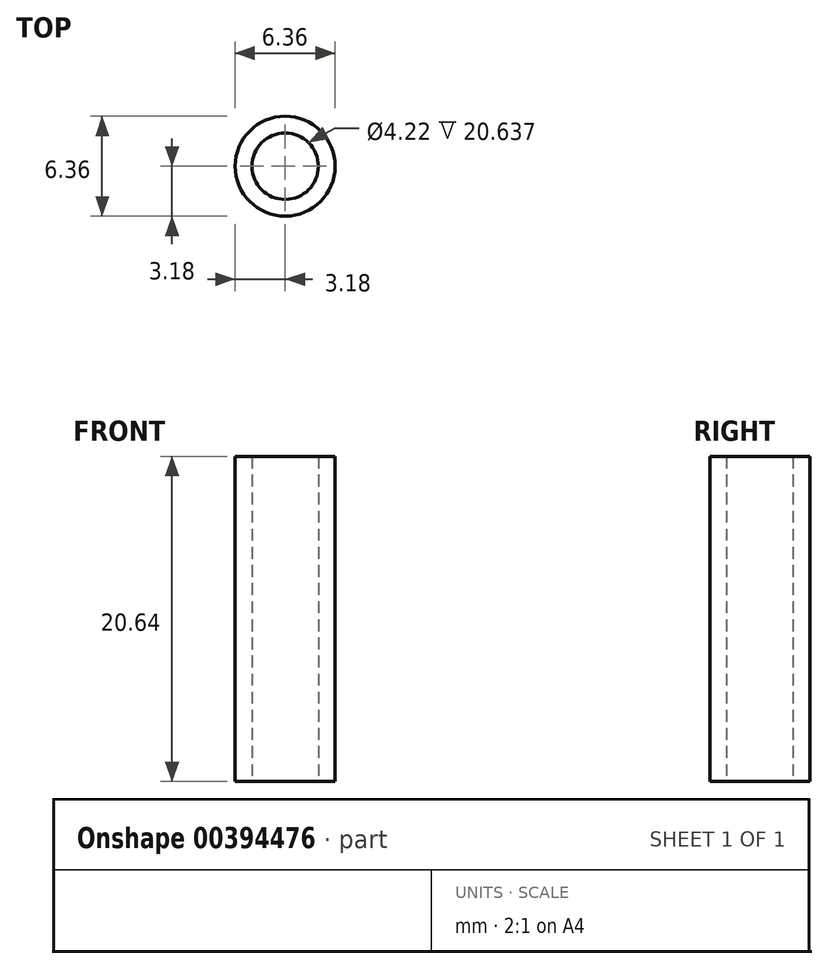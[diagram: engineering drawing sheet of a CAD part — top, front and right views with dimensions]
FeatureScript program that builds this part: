
annotation { "Feature Type Name" : "Feature", "Feature Type Description" : "" }
export const myFeature = defineFeature(function(context is Context, id is Id, definition is map)
    precondition{}
    {
        {
            var Q0;
            Q0=qCreatedBy(makeId("Top.planeOp"),FACE);
            var sketch = newSketch(context, id + "F0", { "sketchPlane" : qUnion([Q0])});
            skCircle(sketch, "E0", {"center": v(0, 0) * mm, "radius": 3.18 * mm});
            skCircle(sketch, "E1", {"center": v(0, 0) * mm, "radius": 2.1 * mm});
            skSolve(sketch);
        }
        {
            var Q0;
            Q0=makeQuery(id+"F0.imprint","IMPRINT",FACE,{"disambiguationData":[TD([[makeQuery(id+"F0.imprint","IMPRINT",EDGE,{"derivedFrom":sQuery(id+"F0.wireOp",EDGE,"E0")}),1.0]])]});
            extrude(context, id + "F1", {"entities" : qUnion([Q0]), "depth" : 20.64 * mm});
        }
    });
